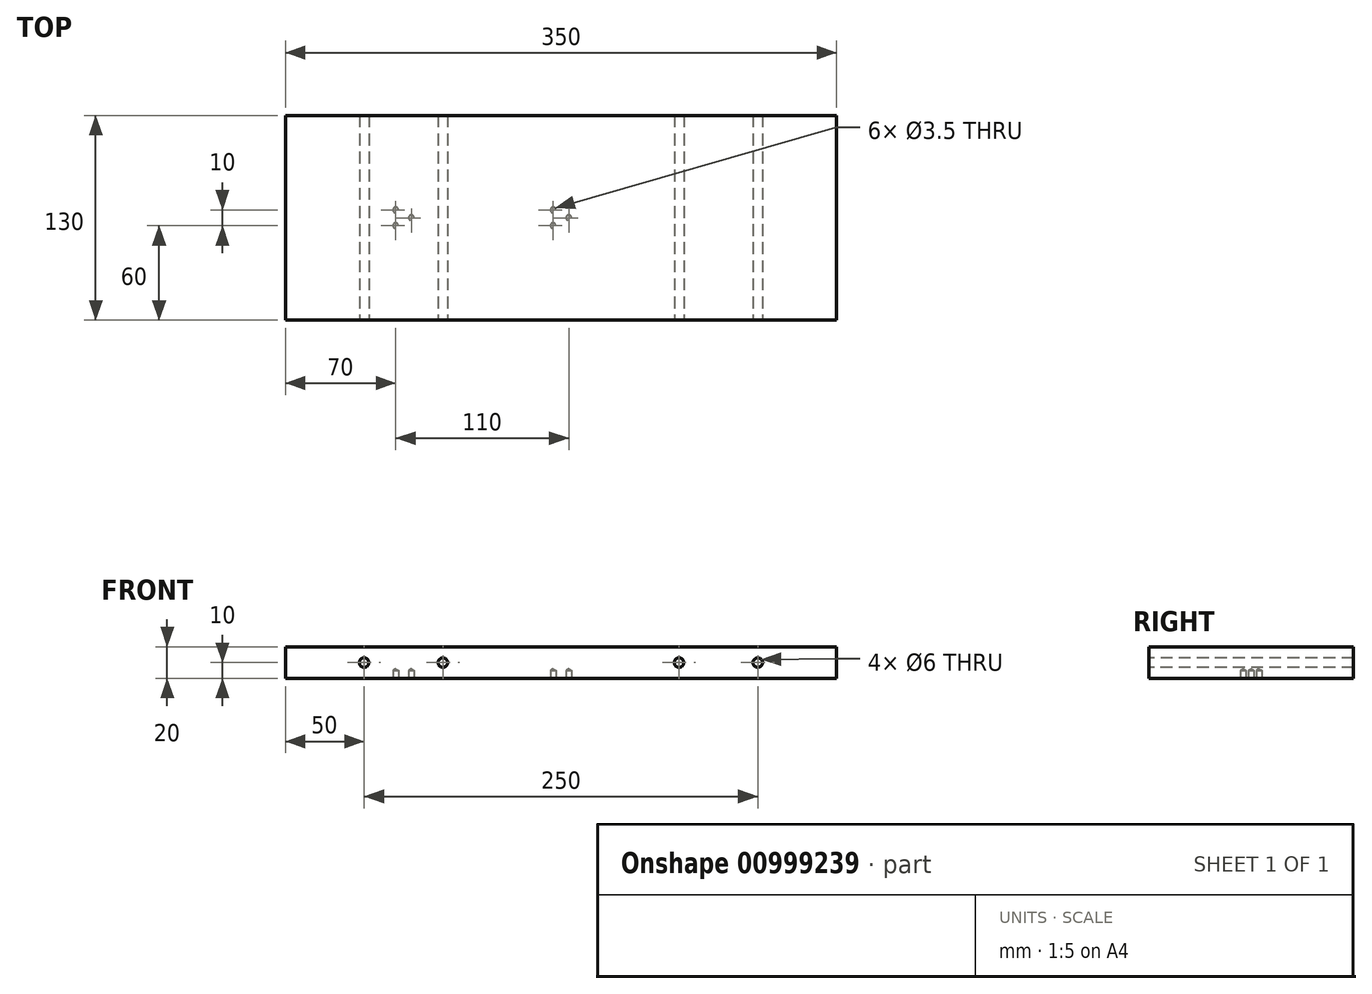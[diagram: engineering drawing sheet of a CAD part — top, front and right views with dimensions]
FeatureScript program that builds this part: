
annotation { "Feature Type Name" : "Feature", "Feature Type Description" : "" }
export const myFeature = defineFeature(function(context is Context, id is Id, definition is map)
    precondition{}
    {
        {
            var Q0;
            Q0=qCreatedBy(makeId("Top.planeOp"),FACE);
            var sketch = newSketch(context, id + "F0", { "sketchPlane" : qUnion([Q0])});
            skLineSegment(sketch, "E0.bottom", {"start": v(175, 65) * mm, "end": v(-175, 65) * mm});
            skLineSegment(sketch, "E0.top", {"start": v(175, -65) * mm, "end": v(-175, -65) * mm});
            skLineSegment(sketch, "E0.left", {"start": v(175, 65) * mm, "end": v(175, -65) * mm});
            skLineSegment(sketch, "E0.right", {"start": v(-175, 65) * mm, "end": v(-175, -65) * mm});
            skPoint(sketch, "E0.middle", {"position": v(0, 0) * mm});
            skSolve(sketch);
        }
        {
            var Q0;
            Q0=qSketchRegion(id+"F0",true);
            extrude(context, id + "F1", {"entities" : qUnion([Q0]), "endBound" : BoundingType.SYMMETRIC, "depth" : 20 * mm, "offsetDistance" : 25 * mm});
        }
        {
            var Q0;
            Q0=makeQuery(id+"F1.opExtrude","SWEPT_FACE",FACE,{"disambiguationData":[OSD([sQuery(id+"F0.wireOp",EDGE,"E0.top")])]});
            var sketch = newSketch(context, id + "F2", { "sketchPlane" : qUnion([Q0])});
            skPoint(sketch, "E1", {"position": v(-125, 0) * mm});
            skPoint(sketch, "E2", {"position": v(-75, 0) * mm});
            skPoint(sketch, "E3", {"position": v(75, 0) * mm});
            skPoint(sketch, "E4", {"position": v(125, 0) * mm});
            skSolve(sketch);
        }
        {
            var Q0;
            Q0=sQuery(id+"F2.wireOp",VERTEX,"E1");
            var Q1;
            Q1=sQuery(id+"F2.wireOp",VERTEX,"E2");
            var Q2;
            Q2=sQuery(id+"F2.wireOp",VERTEX,"E3");
            var Q3;
            Q3=sQuery(id+"F2.wireOp",VERTEX,"E4");
            var Q4;
            Q4=makeQuery(id+"F1.opExtrude","SWEPT_BODY",BODY,{"disambiguationData":[OSD([sQuery(id+"F0.wireOp",EDGE,"E0.bottom"),sQuery(id+"F0.wireOp",EDGE,"E0.top"),sQuery(id+"F0.wireOp",EDGE,"E0.left"),sQuery(id+"F0.wireOp",EDGE,"E0.right")])]});
            hole(context, id + "F3", {"style" : HoleStyle.SIMPLE, "endStyle" : HoleEndStyle.THROUGH, "holeDiameter" : 6 * mm, "majorDiameter" : 5 * mm, "isTappedThrough" : true, "tappedDepth" : 12 * mm, "tapClearance" : 3, "locations" : qUnion([Q0, Q1, Q2, Q3]), "scope" : qUnion([Q4])});
        }
        {
            var Q0;
            Q0=makeQuery(id+"F1.opExtrude","CAP_FACE",FACE,{"disambiguationData":[OSD([sQuery(id+"F0.wireOp",EDGE,"E0.bottom"),sQuery(id+"F0.wireOp",EDGE,"E0.top"),sQuery(id+"F0.wireOp",EDGE,"E0.left"),sQuery(id+"F0.wireOp",EDGE,"E0.right")])],"isStart":true});
            var sketch = newSketch(context, id + "F4", { "sketchPlane" : qUnion([Q0])});
            skPoint(sketch, "E5", {"position": v(-105, 5) * mm});
            skPoint(sketch, "E6", {"position": v(-105, -5) * mm});
            skPoint(sketch, "E7", {"position": v(-95, 0) * mm});
            skPoint(sketch, "E8", {"position": v(-5, 5) * mm});
            skPoint(sketch, "E9", {"position": v(-5, -5) * mm});
            skPoint(sketch, "E10", {"position": v(5, 0) * mm});
            skSolve(sketch);
        }
        {
            var Q0;
            Q0=sQuery(id+"F4.wireOp",VERTEX,"E5");
            var Q1;
            Q1=sQuery(id+"F4.wireOp",VERTEX,"E6");
            var Q2;
            Q2=sQuery(id+"F4.wireOp",VERTEX,"E7");
            var Q3;
            Q3=sQuery(id+"F4.wireOp",VERTEX,"E8");
            var Q4;
            Q4=sQuery(id+"F4.wireOp",VERTEX,"E9");
            var Q5;
            Q5=sQuery(id+"F4.wireOp",VERTEX,"E10");
            var Q6;
            Q6=makeQuery(id+"F1.opExtrude","SWEPT_BODY",BODY,{"disambiguationData":[OSD([sQuery(id+"F0.wireOp",EDGE,"E0.bottom"),sQuery(id+"F0.wireOp",EDGE,"E0.top"),sQuery(id+"F0.wireOp",EDGE,"E0.left"),sQuery(id+"F0.wireOp",EDGE,"E0.right")])]});
            hole(context, id + "F5", {"style" : HoleStyle.SIMPLE, "endStyle" : HoleEndStyle.BLIND, "holeDiameter" : 3.5 * mm, "majorDiameter" : 5 * mm, "holeDepth" : 5 * mm, "isTappedThrough" : true, "tappedDepth" : 12 * mm, "tapClearance" : 3, "locations" : qUnion([Q0, Q1, Q2, Q3, Q4, Q5]), "scope" : qUnion([Q6])});
        }
    });
